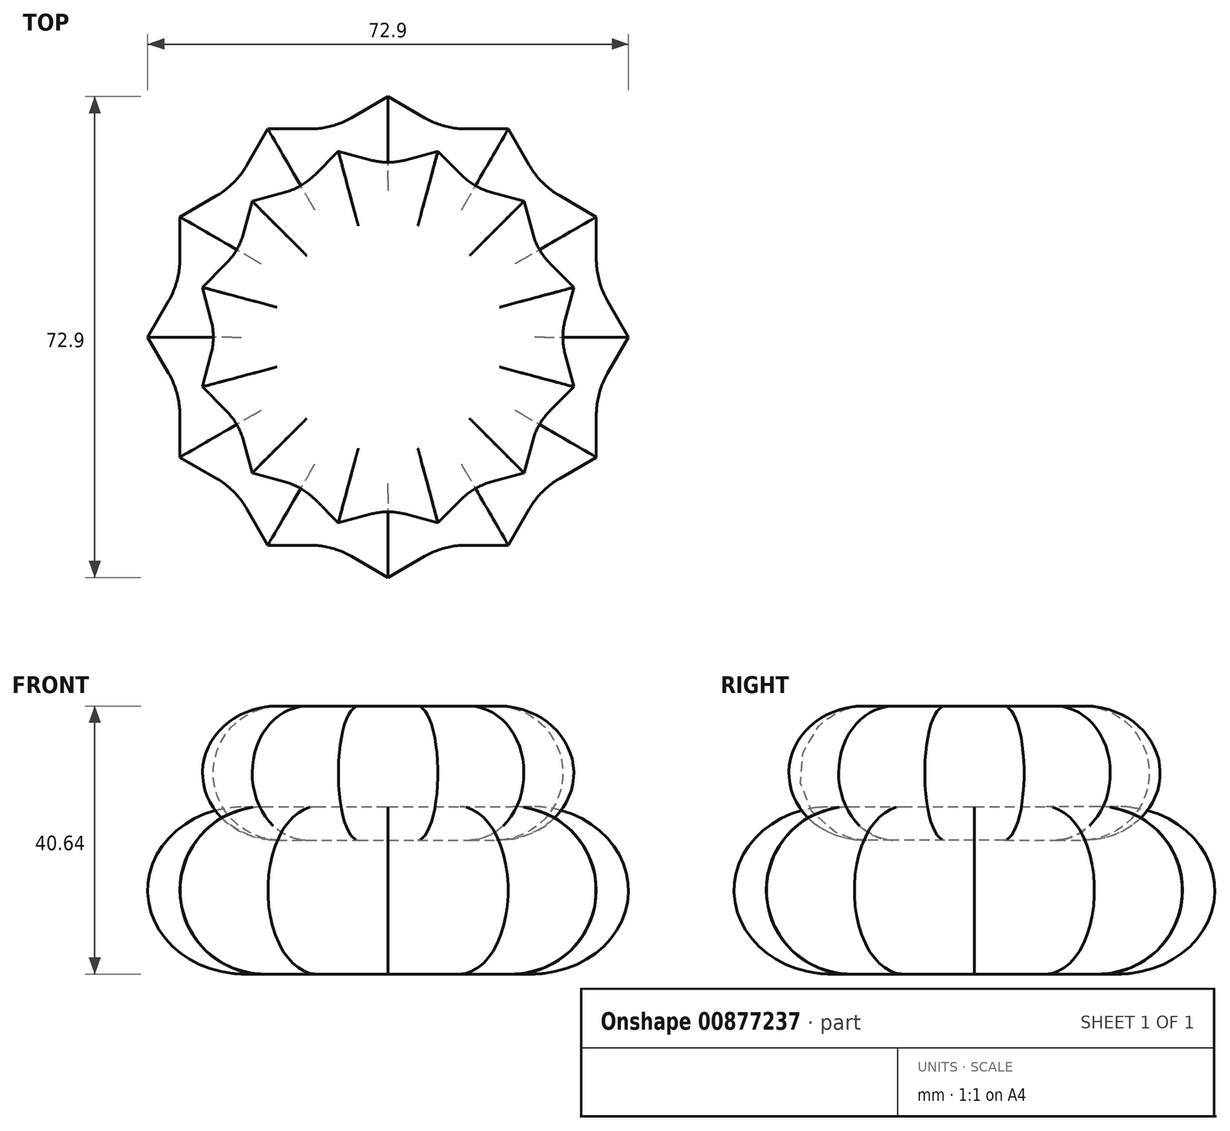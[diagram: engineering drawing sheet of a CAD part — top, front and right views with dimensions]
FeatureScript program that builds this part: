
annotation { "Feature Type Name" : "Feature", "Feature Type Description" : "" }
export const myFeature = defineFeature(function(context is Context, id is Id, definition is map)
    precondition{}
    {
        {
            var Q0;
            Q0=qCreatedBy(makeId("Top.planeOp"),FACE);
            var sketch = newSketch(context, id + "F0", { "sketchPlane" : qUnion([Q0])});
            skCircle(sketch, "E0.cCircle", {"center": v(0, 0) * mm, "radius": 31.57 * mm, "construction": true});
            skLineSegment(sketch, "E0.0", {"start": v(31.57, 18.22) * mm, "end": v(31.57, -18.22) * mm});
            skLineSegment(sketch, "E0.1", {"start": v(31.57, -18.22) * mm, "end": v(0, -36.45) * mm});
            skLineSegment(sketch, "E0.2", {"start": v(0, -36.45) * mm, "end": v(-31.57, -18.22) * mm});
            skLineSegment(sketch, "E0.3", {"start": v(-31.57, -18.22) * mm, "end": v(-31.57, 18.22) * mm});
            skLineSegment(sketch, "E0.4", {"start": v(-31.57, 18.22) * mm, "end": v(0, 36.45) * mm});
            skLineSegment(sketch, "E0.5", {"start": v(0, 36.45) * mm, "end": v(31.57, 18.22) * mm});
            skPoint(sketch, "E0.0.midPoint", {"position": v(31.57, 0) * mm});
            skSolve(sketch);
        }
        {
            var Q0;
            Q0=makeQuery(id+"F0.imprint","IMPRINT",FACE,{"disambiguationData":[TD([[makeQuery(id+"F0.imprint","IMPRINT",EDGE,{"derivedFrom":sQuery(id+"F0.wireOp",EDGE,"E0.0")}),-1.0]])]});
            extrude(context, id + "F1", {"entities" : qUnion([Q0]), "depth" : 25.4 * mm, "offsetDistance" : 25.4 * mm});
        }
        {
            var Q0;
            Q0=makeQuery(id+"F1.opExtrude","CAP_FACE",FACE,{"disambiguationData":[OSD([sQuery(id+"F0.wireOp",EDGE,"E0.0"),sQuery(id+"F0.wireOp",EDGE,"E0.1"),sQuery(id+"F0.wireOp",EDGE,"E0.2"),sQuery(id+"F0.wireOp",EDGE,"E0.3"),sQuery(id+"F0.wireOp",EDGE,"E0.4"),sQuery(id+"F0.wireOp",EDGE,"E0.5")])],"isStart":false});
            var sketch = newSketch(context, id + "F2", { "sketchPlane" : qUnion([Q0])});
            skCircle(sketch, "E1.cCircle", {"center": v(0, 0) * mm, "radius": 31.57 * mm, "construction": true});
            skLineSegment(sketch, "E1.0", {"start": v(-18.22, 31.57) * mm, "end": v(18.22, 31.57) * mm});
            skLineSegment(sketch, "E1.1", {"start": v(18.22, 31.57) * mm, "end": v(36.45, 0) * mm});
            skLineSegment(sketch, "E1.2", {"start": v(36.45, 0) * mm, "end": v(18.22, -31.57) * mm});
            skLineSegment(sketch, "E1.3", {"start": v(18.22, -31.57) * mm, "end": v(-18.22, -31.57) * mm});
            skLineSegment(sketch, "E1.4", {"start": v(-18.22, -31.57) * mm, "end": v(-36.45, 0) * mm});
            skLineSegment(sketch, "E1.5", {"start": v(-36.45, 0) * mm, "end": v(-18.22, 31.57) * mm});
            skPoint(sketch, "E1.0.midPoint", {"position": v(0, 31.57) * mm});
            skSolve(sketch);
        }
        {
            var Q0;
            Q0 = qSketchRegion(id + "F2", true);
            var Q1;
            Q1=sQuery(id+"F0.wireOp",VERTEX,"E0.4.end");
            extrude(context, id + "F3", {"entities" : qUnion([Q0]), "operationType" : NewBodyOperationType.ADD, "endBound" : BoundingType.UP_TO_VERTEX, "oppositeDirection" : true, "depth" : 25.4 * mm, "endBoundEntityVertex" : qUnion([Q1]), "offsetDistance" : 25.4 * mm});
        }
        {
            var Q0;
            Q0=makeQuery(id+"F3.boolean.opBoolean","INTERSECT",EDGE,{"derivedFrom":[makeQuery(id+"F1.opExtrude","SWEPT_FACE",FACE,{"disambiguationData":[OSD([sQuery(id+"F0.wireOp",EDGE,"E0.3")])]}),makeQuery(id+"F3.opExtrude","SWEPT_FACE",FACE,{"disambiguationData":[OSD([sQuery(id+"F2.wireOp",EDGE,"E1.4")])]})]});
            var Q1;
            Q1=makeQuery(id+"F3.boolean.opBoolean","INTERSECT",EDGE,{"derivedFrom":[makeQuery(id+"F1.opExtrude","SWEPT_FACE",FACE,{"disambiguationData":[OSD([sQuery(id+"F0.wireOp",EDGE,"E0.2")])]}),makeQuery(id+"F3.opExtrude","SWEPT_FACE",FACE,{"disambiguationData":[OSD([sQuery(id+"F2.wireOp",EDGE,"E1.4")])]})]});
            var Q2;
            Q2=makeQuery(id+"F3.boolean.opBoolean","INTERSECT",EDGE,{"derivedFrom":[makeQuery(id+"F1.opExtrude","SWEPT_FACE",FACE,{"disambiguationData":[OSD([sQuery(id+"F0.wireOp",EDGE,"E0.2")])]}),makeQuery(id+"F3.opExtrude","SWEPT_FACE",FACE,{"disambiguationData":[OSD([sQuery(id+"F2.wireOp",EDGE,"E1.3")])]})]});
            var Q3;
            Q3=makeQuery(id+"F3.boolean.opBoolean","INTERSECT",EDGE,{"derivedFrom":[makeQuery(id+"F1.opExtrude","SWEPT_FACE",FACE,{"disambiguationData":[OSD([sQuery(id+"F0.wireOp",EDGE,"E0.1")])]}),makeQuery(id+"F3.opExtrude","SWEPT_FACE",FACE,{"disambiguationData":[OSD([sQuery(id+"F2.wireOp",EDGE,"E1.3")])]})]});
            var Q4;
            Q4=makeQuery(id+"F3.boolean.opBoolean","INTERSECT",EDGE,{"derivedFrom":[makeQuery(id+"F1.opExtrude","SWEPT_FACE",FACE,{"disambiguationData":[OSD([sQuery(id+"F0.wireOp",EDGE,"E0.1")])]}),makeQuery(id+"F3.opExtrude","SWEPT_FACE",FACE,{"disambiguationData":[OSD([sQuery(id+"F2.wireOp",EDGE,"E1.2")])]})]});
            var Q5;
            Q5=makeQuery(id+"F3.boolean.opBoolean","INTERSECT",EDGE,{"derivedFrom":[makeQuery(id+"F1.opExtrude","SWEPT_FACE",FACE,{"disambiguationData":[OSD([sQuery(id+"F0.wireOp",EDGE,"E0.0")])]}),makeQuery(id+"F3.opExtrude","SWEPT_FACE",FACE,{"disambiguationData":[OSD([sQuery(id+"F2.wireOp",EDGE,"E1.2")])]})]});
            var Q6;
            Q6=makeQuery(id+"F3.boolean.opBoolean","INTERSECT",EDGE,{"derivedFrom":[makeQuery(id+"F1.opExtrude","SWEPT_FACE",FACE,{"disambiguationData":[OSD([sQuery(id+"F0.wireOp",EDGE,"E0.0")])]}),makeQuery(id+"F3.opExtrude","SWEPT_FACE",FACE,{"disambiguationData":[OSD([sQuery(id+"F2.wireOp",EDGE,"E1.1")])]})]});
            var Q7;
            Q7=makeQuery(id+"F3.boolean.opBoolean","INTERSECT",EDGE,{"derivedFrom":[makeQuery(id+"F1.opExtrude","SWEPT_FACE",FACE,{"disambiguationData":[OSD([sQuery(id+"F0.wireOp",EDGE,"E0.5")])]}),makeQuery(id+"F3.opExtrude","SWEPT_FACE",FACE,{"disambiguationData":[OSD([sQuery(id+"F2.wireOp",EDGE,"E1.1")])]})]});
            var Q8;
            Q8=makeQuery(id+"F3.boolean.opBoolean","INTERSECT",EDGE,{"derivedFrom":[makeQuery(id+"F1.opExtrude","SWEPT_FACE",FACE,{"disambiguationData":[OSD([sQuery(id+"F0.wireOp",EDGE,"E0.5")])]}),makeQuery(id+"F3.opExtrude","SWEPT_FACE",FACE,{"disambiguationData":[OSD([sQuery(id+"F2.wireOp",EDGE,"E1.0")])]})]});
            var Q9;
            Q9=makeQuery(id+"F3.boolean.opBoolean","INTERSECT",EDGE,{"derivedFrom":[makeQuery(id+"F1.opExtrude","SWEPT_FACE",FACE,{"disambiguationData":[OSD([sQuery(id+"F0.wireOp",EDGE,"E0.4")])]}),makeQuery(id+"F3.opExtrude","SWEPT_FACE",FACE,{"disambiguationData":[OSD([sQuery(id+"F2.wireOp",EDGE,"E1.0")])]})]});
            var Q10;
            Q10=makeQuery(id+"F3.boolean.opBoolean","INTERSECT",EDGE,{"derivedFrom":[makeQuery(id+"F1.opExtrude","SWEPT_FACE",FACE,{"disambiguationData":[OSD([sQuery(id+"F0.wireOp",EDGE,"E0.4")])]}),makeQuery(id+"F3.opExtrude","SWEPT_FACE",FACE,{"disambiguationData":[OSD([sQuery(id+"F2.wireOp",EDGE,"E1.5")])]})]});
            var Q11;
            Q11=makeQuery(id+"F3.boolean.opBoolean","INTERSECT",EDGE,{"derivedFrom":[makeQuery(id+"F1.opExtrude","SWEPT_FACE",FACE,{"disambiguationData":[OSD([sQuery(id+"F0.wireOp",EDGE,"E0.3")])]}),makeQuery(id+"F3.opExtrude","SWEPT_FACE",FACE,{"disambiguationData":[OSD([sQuery(id+"F2.wireOp",EDGE,"E1.5")])]})]});
            fillet(context, id + "F4", {"entities" : qUnion([Q0, Q1, Q2, Q3, Q4, Q5, Q6, Q7, Q8, Q9, Q10, Q11]), "radius" : 12.7 * mm, "tangentPropagation" : true, "allowEdgeOverflow" : false});
        }
        {
            var Q0;
            Q0=makeQuery(id+"F3.boolean.opBoolean","MERGE",FACE,{"derivedFrom":[makeQuery(id+"F1.opExtrude","CAP_FACE",FACE,{"disambiguationData":[OSD([sQuery(id+"F0.wireOp",EDGE,"E0.0"),sQuery(id+"F0.wireOp",EDGE,"E0.1"),sQuery(id+"F0.wireOp",EDGE,"E0.2"),sQuery(id+"F0.wireOp",EDGE,"E0.3"),sQuery(id+"F0.wireOp",EDGE,"E0.4"),sQuery(id+"F0.wireOp",EDGE,"E0.5")])],"isStart":false}),makeQuery(id+"F3.opExtrude","CAP_FACE",FACE,{"disambiguationData":[OSD([sQuery(id+"F2.wireOp",EDGE,"E1.0"),sQuery(id+"F2.wireOp",EDGE,"E1.1"),sQuery(id+"F2.wireOp",EDGE,"E1.2"),sQuery(id+"F2.wireOp",EDGE,"E1.3"),sQuery(id+"F2.wireOp",EDGE,"E1.4"),sQuery(id+"F2.wireOp",EDGE,"E1.5")])],"isStart":true})]});
            var Q1;
            Q1=makeQuery(id+"F3.boolean.opBoolean","MERGE",FACE,{"derivedFrom":[makeQuery(id+"F1.opExtrude","CAP_FACE",FACE,{"disambiguationData":[OSD([sQuery(id+"F0.wireOp",EDGE,"E0.0"),sQuery(id+"F0.wireOp",EDGE,"E0.1"),sQuery(id+"F0.wireOp",EDGE,"E0.2"),sQuery(id+"F0.wireOp",EDGE,"E0.3"),sQuery(id+"F0.wireOp",EDGE,"E0.4"),sQuery(id+"F0.wireOp",EDGE,"E0.5")])],"isStart":true}),makeQuery(id+"F3.opExtrude","CAP_FACE",FACE,{"disambiguationData":[OSD([sQuery(id+"F2.wireOp",EDGE,"E1.0"),sQuery(id+"F2.wireOp",EDGE,"E1.1"),sQuery(id+"F2.wireOp",EDGE,"E1.2"),sQuery(id+"F2.wireOp",EDGE,"E1.3"),sQuery(id+"F2.wireOp",EDGE,"E1.4"),sQuery(id+"F2.wireOp",EDGE,"E1.5")])],"isStart":false})]});
            fillet(context, id + "F5", {"entities" : qUnion([Q0, Q1]), "radius" : 12.7 * mm, "tangentPropagation" : true, "allowEdgeOverflow" : false});
        }
        {
            var Q0;
            Q0=makeQuery(id+"F1.opExtrude","SWEPT_BODY",BODY,{"disambiguationData":[OSD([sQuery(id+"F0.wireOp",EDGE,"E0.0"),sQuery(id+"F0.wireOp",EDGE,"E0.1"),sQuery(id+"F0.wireOp",EDGE,"E0.2"),sQuery(id+"F0.wireOp",EDGE,"E0.3"),sQuery(id+"F0.wireOp",EDGE,"E0.4"),sQuery(id+"F0.wireOp",EDGE,"E0.5")])]});
            transform(context, id + "F6", {"entities" : qUnion([Q0]), "transformType" : TransformType.TRANSLATION_3D, "dx" : 0 * mm, "dy" : 0 * mm, "dz" : 25.4 * mm, "makeCopy" : true});
        }
        {
            var Q0;
            Q0=makeQuery(id+"F6.opPattern","COPY",BODY,{"derivedFrom":makeQuery(id+"F1.opExtrude","SWEPT_BODY",BODY,{"disambiguationData":[OSD([sQuery(id+"F0.wireOp",EDGE,"E0.0"),sQuery(id+"F0.wireOp",EDGE,"E0.1"),sQuery(id+"F0.wireOp",EDGE,"E0.2"),sQuery(id+"F0.wireOp",EDGE,"E0.3"),sQuery(id+"F0.wireOp",EDGE,"E0.4"),sQuery(id+"F0.wireOp",EDGE,"E0.5")])]}),"instanceName":"1"});
            var Q1;
            Q1=sQuery(id+"F0.wireOp",VERTEX,"E0.cCircle.center");
            transform(context, id + "F7", {"entities" : qUnion([Q0]), "transformType" : TransformType.SCALE_UNIFORMLY, "scale" : .8, "scalePoint" : qUnion([Q1]), "makeCopy" : false});
        }
        {
            var Q0;
            Q0=qCreatedBy(makeId("Right.planeOp"),FACE);
            var sketch = newSketch(context, id + "F8", { "sketchPlane" : qUnion([Q0])});
            skLineSegment(sketch, "E2", {"start": v(0, 0) * mm, "end": v(0, 75.79) * mm});
            skSolve(sketch);
        }
        {
            var Q0;
            Q0=makeQuery(id+"F6.opPattern","COPY",BODY,{"derivedFrom":makeQuery(id+"F1.opExtrude","SWEPT_BODY",BODY,{"disambiguationData":[OSD([sQuery(id+"F0.wireOp",EDGE,"E0.0"),sQuery(id+"F0.wireOp",EDGE,"E0.1"),sQuery(id+"F0.wireOp",EDGE,"E0.2"),sQuery(id+"F0.wireOp",EDGE,"E0.3"),sQuery(id+"F0.wireOp",EDGE,"E0.4"),sQuery(id+"F0.wireOp",EDGE,"E0.5")])]}),"instanceName":"1"});
            var Q1;
            Q1=sQuery(id+"F8.wireOp",EDGE,"E2");
            transform(context, id + "F9", {"entities" : qUnion([Q0]), "transformType" : TransformType.ROTATION, "transformAxis" : qUnion([Q1]), "angle" : 45 * degree, "makeCopy" : false});
        }
    });
